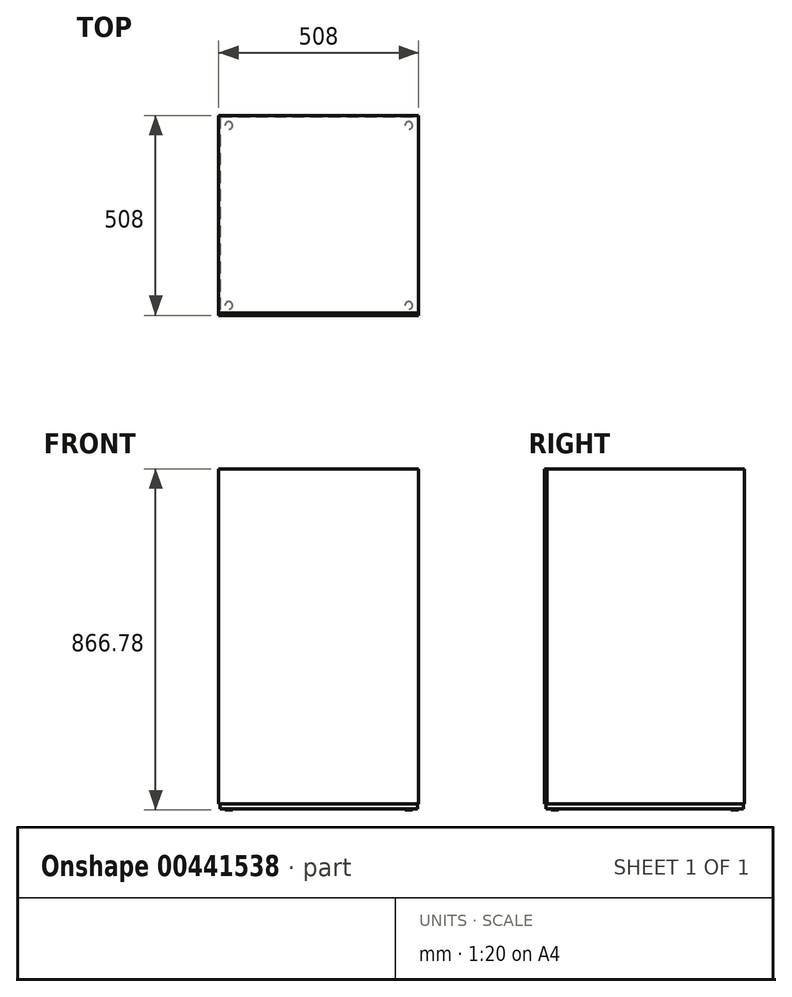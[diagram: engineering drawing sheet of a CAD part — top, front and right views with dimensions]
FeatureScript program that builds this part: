
annotation { "Feature Type Name" : "Feature", "Feature Type Description" : "" }
export const myFeature = defineFeature(function(context is Context, id is Id, definition is map)
    precondition{}
    {
        {
            var Q0;
            Q0=qCreatedBy(makeId("Top.planeOp"),FACE);
            var sketch = newSketch(context, id + "F0", { "sketchPlane" : qUnion([Q0])});
            skLineSegment(sketch, "E0.bottom", {"start": v(-250.83, 250.83) * mm, "end": v(250.83, 250.83) * mm});
            skLineSegment(sketch, "E0.top", {"start": v(-250.83, -250.83) * mm, "end": v(250.83, -250.83) * mm});
            skLineSegment(sketch, "E0.left", {"start": v(-250.82, 250.83) * mm, "end": v(-250.83, -250.83) * mm});
            skLineSegment(sketch, "E0.right", {"start": v(250.83, 250.83) * mm, "end": v(250.82, -250.83) * mm});
            skLineSegment(sketch, "E1", {"start": v(0, 250.82) * mm, "end": v(0, -250.82) * mm, "construction": true});
            skLineSegment(sketch, "E2", {"start": v(-250.83, 0) * mm, "end": v(250.83, 0) * mm, "construction": true});
            skPoint(sketch, "E3", {"position": v(0, 0) * mm});
            skSolve(sketch);
        }
        {
            var Q0;
            Q0 = qSketchRegion(id + "F0", true);
            extrude(context, id + "F1", {"entities" : qUnion([Q0]), "depth" : 12.7 * mm});
        }
        {
            var Q0;
            Q0=makeQuery(id+"F1.opExtrude","CAP_FACE",FACE,{"disambiguationData":[OSD([sQuery(id+"F0.wireOp",EDGE,"E0.bottom"),sQuery(id+"F0.wireOp",EDGE,"E0.top"),sQuery(id+"F0.wireOp",EDGE,"E0.left"),sQuery(id+"F0.wireOp",EDGE,"E0.right")])],"isStart":false});
            var sketch = newSketch(context, id + "F2", { "sketchPlane" : qUnion([Q0])});
            skLineSegment(sketch, "E4.0", {"start": v(-254, 254) * mm, "end": v(-254, -254) * mm});
            skLineSegment(sketch, "E4.1", {"start": v(-254, 254) * mm, "end": v(254, 254) * mm});
            skLineSegment(sketch, "E4.2", {"start": v(254, 254) * mm, "end": v(254, -254) * mm});
            skLineSegment(sketch, "E4.3", {"start": v(-254, -254) * mm, "end": v(254, -254) * mm});
            skLineSegment(sketch, "E5", {"start": v(-254, -247.65) * mm, "end": v(254, -247.65) * mm});
            skSolve(sketch);
        }
        {
            var Q0;
            {var subQ5=makeQuery(id+"F1.opExtrude","CAP_EDGE",EDGE,{"disambiguationData":[OSD([sQuery(id+"F0.wireOp",EDGE,"E0.bottom")])],"isStart":false});Q0=makeQuery(id+"F2.imprint","IMPRINT",FACE,{"disambiguationData":[TD([[makeQuery(id+"F2.imprint","IMPRINT",EDGE,{"derivedFrom":subQ5}),-1.0]])]});}
            var Q1;
            {var subQ6=sQuery(id+"F2.wireOp",EDGE,"E4.1");Q1=makeQuery(id+"F2.imprint","IMPRINT",FACE,{"disambiguationData":[TD([[makeQuery(id+"F2.imprint","IMPRINT",EDGE,{"derivedFrom":subQ6}),-1.0]])]});}
            extrude(context, id + "F3", {"entities" : qUnion([Q0, Q1]), "operationType" : NewBodyOperationType.ADD, "depth" : 850.9 * mm});
        }
        {
            var Q0;
            {var subQ5=makeQuery(id+"F1.opExtrude","CAP_EDGE",EDGE,{"disambiguationData":[OSD([sQuery(id+"F0.wireOp",EDGE,"E0.top")])],"isStart":false});Q0=makeQuery(id+"F2.imprint","IMPRINT",FACE,{"disambiguationData":[TD([[makeQuery(id+"F2.imprint","IMPRINT",EDGE,{"derivedFrom":subQ5}),1.0]])]});}
            var Q1;
            {var subQ0=sQuery(id+"F2.wireOp",EDGE,"E4.3");Q1=makeQuery(id+"F2.imprint","IMPRINT",FACE,{"disambiguationData":[TD([[makeQuery(id+"F2.imprint","IMPRINT",EDGE,{"derivedFrom":subQ0}),1.0]])]});}
            extrude(context, id + "F4", {"entities" : qUnion([Q0, Q1]), "depth" : 850.9 * mm});
        }
        {
            var Q0;
            Q0=makeQuery(id+"F1.opExtrude","CAP_FACE",FACE,{"disambiguationData":[OSD([sQuery(id+"F0.wireOp",EDGE,"E0.bottom"),sQuery(id+"F0.wireOp",EDGE,"E0.top"),sQuery(id+"F0.wireOp",EDGE,"E0.left"),sQuery(id+"F0.wireOp",EDGE,"E0.right")])],"isStart":true});
            var sketch = newSketch(context, id + "F5", { "sketchPlane" : qUnion([Q0])});
            skPoint(sketch, "E6", {"position": v(0, 0) * mm});
            skCircle(sketch, "E7", {"center": v(-228.6, 228.6) * mm, "radius": 9.53 * mm});
            skCircle(sketch, "E8.0.1.0", {"center": v(-228.6, -228.6) * mm, "radius": 9.53 * mm});
            skCircle(sketch, "E8.1.0.0", {"center": v(228.6, 228.6) * mm, "radius": 9.53 * mm});
            skCircle(sketch, "E8.1.1.0", {"center": v(228.6, -228.6) * mm, "radius": 9.53 * mm});
            skLineSegment(sketch, "E8.direction1", {"start": v(-228.6, 228.6) * mm, "end": v(228.6, 228.6) * mm, "construction": true});
            skLineSegment(sketch, "E8.direction2", {"start": v(-228.6, 228.6) * mm, "end": v(-228.6, -228.6) * mm, "construction": true});
            skSolve(sketch);
        }
        {
            var Q0;
            Q0 = qSketchRegion(id + "F5", true);
            extrude(context, id + "F6", {"entities" : qUnion([Q0]), "depth" : 3.17 * mm});
        }
    });
